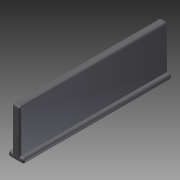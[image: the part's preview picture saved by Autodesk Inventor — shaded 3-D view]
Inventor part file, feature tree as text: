
AUTODESK INVENTOR PART (.ipt)
format: ipt  version: 2013 (Build 170138000, 138)  size: 107,008 bytes
history: native  units: in
note: dims shown in document units (in); Inventor stores cm internally (conversion verified against a paired STEP export)
features: extrude x1, fillet x1, sketch x1
ambient origin geometry x8: Origin, YZ Plane, XZ Plane, XY Plane, X Axis, Y Axis, Z Axis, Center Point
bodies: Solid1 (feature_tree)
feature tree (3):
  extrude  "Extrusion1"  Depth=0.1575in
  fillet  "Fillet1"  Radius=0.0512in
  sketch  "Sketch1"  dims[d0=0.484in d1=0.1575in d2=0.0512in d3=0.0394in d4=0.0394in d5=1.496in d6=0.0in d7=0.02in]
